# Revit family: 305_A55H_
name_source: partatom
category: Pipe Accessories
revit_build: Autodesk Revit 2018 (Build: 20170223_1515(x64)
units: mm (PartAtom-declared; Revit-internal decimal feet)

## family parameters
Always vertical = Yes
Cut with Voids When Loaded = No
Part Type = Valve - Breaks Into
Round Connector Dimension = Use Diameter
Shared = No
Work Plane-Based = No

## types (2) — shared parameters
A2 = 65 mm  [stored 0.213255 ft]
BH = 67 mm  [stored 0.219816 ft]
CAT0 = Yes
D = 65 mm
Description = MALE THREAD ANGLE HOSE VALVE
HB = 98 mm
HH = 25 mm  [stored 0.082021 ft]
HH__ve = -25 mm  [stored -0.082021 ft]
HN = 28 mm  [stored 0.0918635 ft]
HP = 30 mm
HP__ve = -30 mm
HT = 229 mm
L = 80 mm
L2D = 80 mm
L2D_Min = 3048 mm  [stored 10 ft]
Manufacturer = Giacomini
QmdConnectorList = 301;D;302;D
R1 = 20 mm  [stored 0.0656168 ft]
R12 = 10 mm  [stored 0.0328084 ft]
RB = 56 mm
RN = 47 mm
RP = 39 mm  [stored 0.127953 ft]
TH = 136 mm
URL = http://www.giacomini.com
W2D = 65 mm  [stored 0.213255 ft]
magiPartTypeId = 305
magiProductFamilyId = A55H*
zero-valued in all types: MC_Default_elevation

## type names (no varying parameters)
- A55HY005
- A55H015

note: column(s) folded — value = type name in every type: magiProductCode, magiProductId

note: [stored X ft] marks values corroborated as IEEE doubles in the binary element streams (Revit-internal decimal feet)

## geometry (parser evidence)
native form markers: Sweep x3
no freeform markers — native parametric forms only
